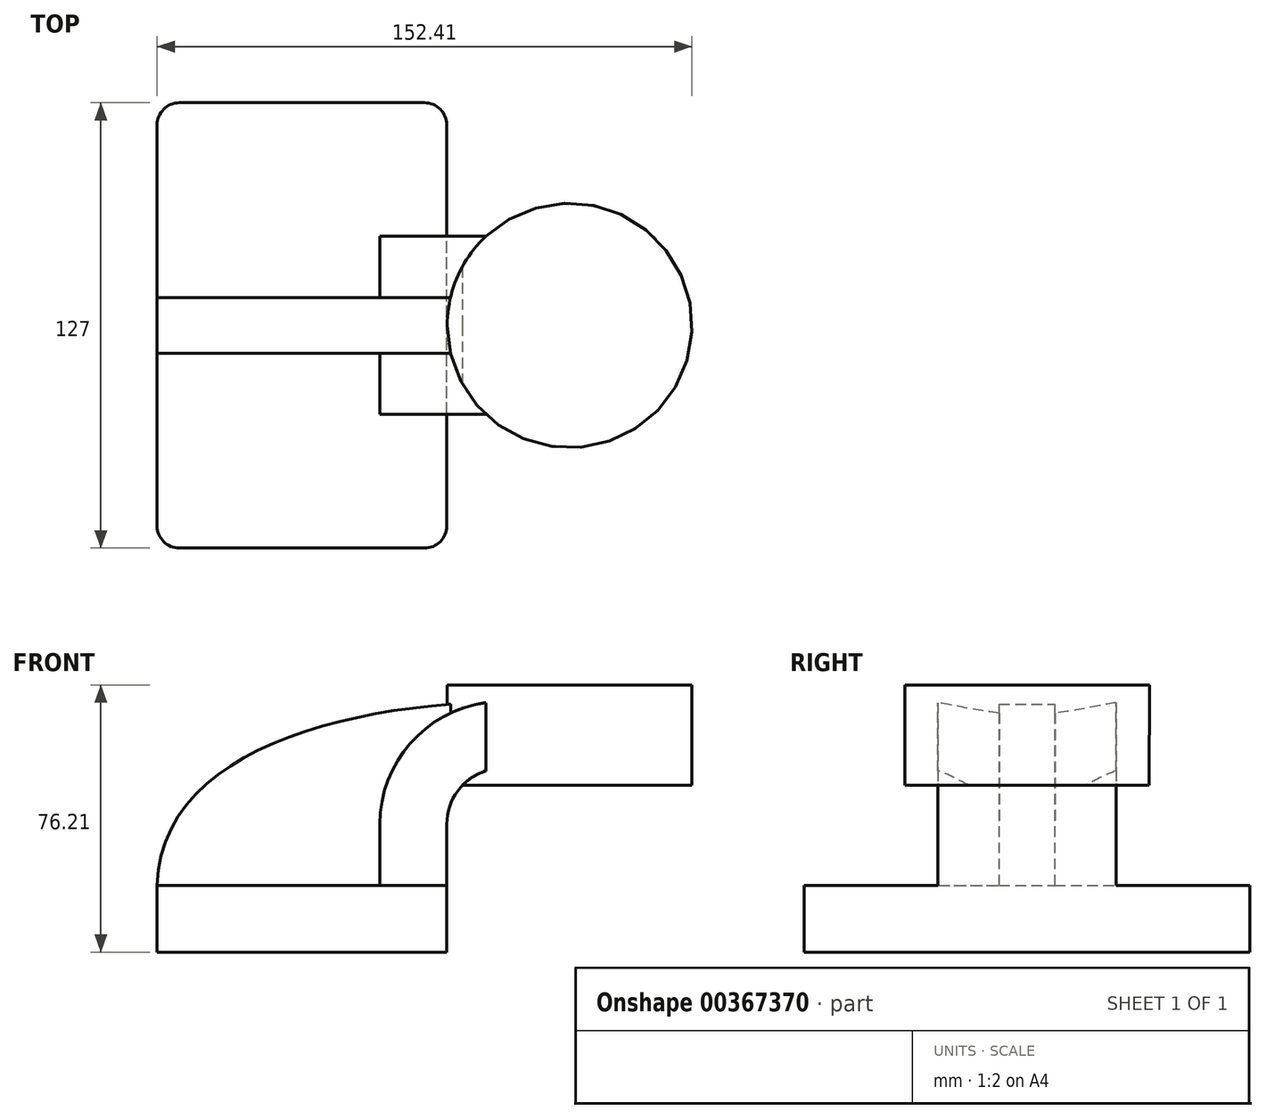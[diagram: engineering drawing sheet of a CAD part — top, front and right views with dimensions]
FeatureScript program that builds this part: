
annotation { "Feature Type Name" : "Feature", "Feature Type Description" : "" }
export const myFeature = defineFeature(function(context is Context, id is Id, definition is map)
    precondition{}
    {
        {
            var Q0;
            Q0=qCreatedBy(makeId("Front.planeOp"),FACE);
            var sketch = newSketch(context, id + "F0", { "sketchPlane" : qUnion([Q0])});
            skLineSegment(sketch, "E0.bottom", {"start": v(-41.27, -9.53) * mm, "end": v(41.28, -9.53) * mm});
            skLineSegment(sketch, "E0.top", {"start": v(-41.28, 9.53) * mm, "end": v(41.28, 9.53) * mm});
            skLineSegment(sketch, "E0.left", {"start": v(-41.28, -9.53) * mm, "end": v(-41.28, 9.53) * mm});
            skLineSegment(sketch, "E0.right", {"start": v(41.28, -9.53) * mm, "end": v(41.28, 9.52) * mm});
            skPoint(sketch, "E0.middle", {"position": v(0, 0) * mm});
            skLineSegment(sketch, "E1.bottom", {"start": v(111.12, 66.67) * mm, "end": v(60.32, 66.67) * mm});
            skLineSegment(sketch, "E1.top", {"start": v(111.12, 38.1) * mm, "end": v(60.33, 38.1) * mm});
            skLineSegment(sketch, "E1.left", {"start": v(111.12, 66.68) * mm, "end": v(111.12, 38.1) * mm});
            skLineSegment(sketch, "E1.right", {"start": v(60.32, 66.68) * mm, "end": v(60.33, 38.1) * mm});
            skPoint(sketch, "E1.middle", {"position": v(85.72, 52.39) * mm});
            skLineSegment(sketch, "E2", {"start": v(41.28, 9.52) * mm, "end": v(41.28, 27) * mm});
            skArc(sketch, "E3", {"start": v(41.27, 27) * mm, "mid": v(45.92, 38.23) * mm, "end": v(57.15, 42.88) * mm});
            skLineSegment(sketch, "E4", {"start": v(57.15, 42.88) * mm, "end": v(76.26, 42.88) * mm});
            skLineSegment(sketch, "E5.0", {"start": v(57.15, 61.93) * mm, "end": v(76.26, 61.93) * mm});
            skArc(sketch, "E5.1", {"start": v(22.23, 27) * mm, "mid": v(32.45, 51.7) * mm, "end": v(57.15, 61.93) * mm});
            skLineSegment(sketch, "E5.2", {"start": v(22.23, 9.52) * mm, "end": v(22.23, 27) * mm});
            skLineSegment(sketch, "E6", {"start": v(76.3, 38.1) * mm, "end": v(76.26, 66.67) * mm});
            skFitSpline(sketch, "E7", {"points": [v(-41.28, 9.53) * mm, v(57.15, 61.93) * mm], "startDerivative": vector(3.52, 115.3) * mm, "endDerivative": vector(136.31, 2.86) * mm});
            skSolve(sketch);
        }
        {
            var Q0;
            Q0=makeQuery(id+"F0.imprint","IMPRINT",FACE,{"disambiguationData":[TD([[makeQuery(id+"F0.imprint","IMPRINT",EDGE,{"derivedFrom":sQuery(id+"F0.wireOp",EDGE,"E0.bottom")}),1.0]])]});
            extrude(context, id + "F1", {"entities" : qUnion([Q0]), "endBound" : BoundingType.SYMMETRIC, "depth" : 127 * mm});
        }
        {
            var Q0;
            {var subQ1=sQuery(id+"F0.wireOp",EDGE,"E2");Q0=makeQuery(id+"F0.imprint","IMPRINT",FACE,{"disambiguationData":[TD([[makeQuery(id+"F0.imprint","IMPRINT",EDGE,{"derivedFrom":subQ1}),1.0]])]});}
            extrude(context, id + "F2", {"entities" : qUnion([Q0]), "operationType" : NewBodyOperationType.ADD, "endBound" : BoundingType.SYMMETRIC, "depth" : 50.8 * mm});
        }
        {
            var Q0;
            Q0=makeQuery(id+"F2.opExtrude","SWEPT_FACE",FACE,{"disambiguationData":[OSD([sQuery(id+"F0.wireOp",EDGE,"E1.right")])]});
            extrude(context, id + "F3", {"entities" : qUnion([Q0]), "operationType" : NewBodyOperationType.ADD, "depth" : 25.4 * mm});
        }
        {
            var Q0;
            {var subQ3=sQuery(id+"F0.wireOp",EDGE,"E5.2");Q0=makeQuery(id+"F0.imprint","IMPRINT",FACE,{"disambiguationData":[TD([[makeQuery(id+"F0.imprint","IMPRINT",EDGE,{"derivedFrom":subQ3}),1.0]])]});}
            extrude(context, id + "F4", {"entities" : qUnion([Q0]), "operationType" : NewBodyOperationType.ADD, "endBound" : BoundingType.SYMMETRIC, "depth" : 15.88 * mm});
        }
        {
            var Q0;
            {var subQ0=sQuery(id+"F0.wireOp",EDGE,"E1.left");Q0=makeQuery(id+"F0.imprint","IMPRINT",FACE,{"disambiguationData":[TD([[makeQuery(id+"F0.imprint","IMPRINT",EDGE,{"derivedFrom":subQ0}),-1.0]])]});}
            var Q1;
            Q1=sQuery(id+"F0.wireOp",EDGE,"E6");
            revolve(context, id + "F5", {"operationType" : NewBodyOperationType.ADD, "entities" : qUnion([Q0]), "axis" : qUnion([Q1]), "revolveType" : RevolveType.FULL});
        }
        {
            var Q0;
            Q0=makeQuery(id+"F1.opExtrude","CAP_EDGE",EDGE,{"disambiguationData":[OSD([sQuery(id+"F0.wireOp",EDGE,"E0.left")])],"isStart":false});
            var Q1;
            Q1=makeQuery(id+"F1.opExtrude","CAP_EDGE",EDGE,{"disambiguationData":[OSD([sQuery(id+"F0.wireOp",EDGE,"E0.right")])],"isStart":false});
            var Q2;
            Q2=makeQuery(id+"F1.opExtrude","CAP_EDGE",EDGE,{"disambiguationData":[OSD([sQuery(id+"F0.wireOp",EDGE,"E0.right")])],"isStart":true});
            var Q3;
            Q3=makeQuery(id+"F1.opExtrude","CAP_EDGE",EDGE,{"disambiguationData":[OSD([sQuery(id+"F0.wireOp",EDGE,"E0.left")])],"isStart":true});
            fillet(context, id + "F6", {"entities" : qUnion([Q0, Q1, Q2, Q3]), "radius" : 6.35 * mm, "tangentPropagation" : true, "allowEdgeOverflow" : false});
        }
    });
